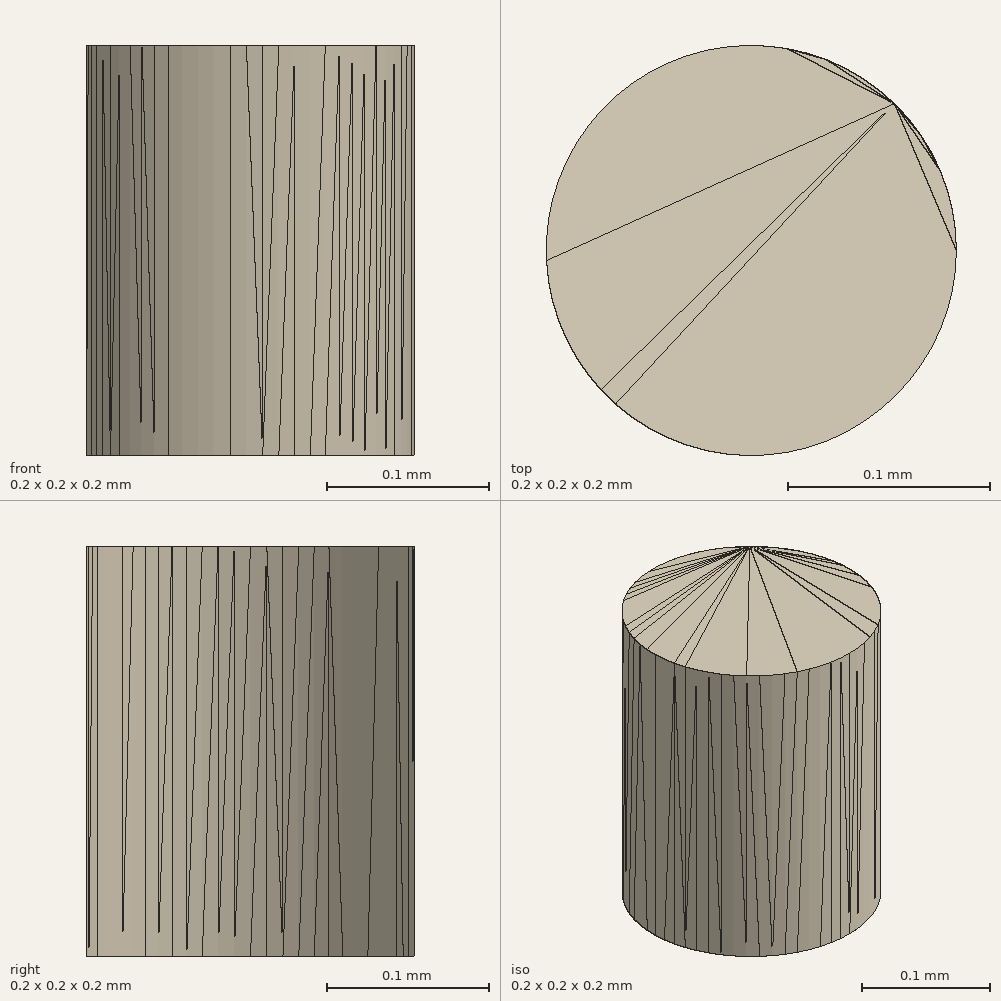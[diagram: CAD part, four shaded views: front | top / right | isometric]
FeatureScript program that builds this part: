
annotation { "Feature Type Name" : "Feature", "Feature Type Description" : "" }
export const myFeature = defineFeature(function(context is Context, id is Id, definition is map)
    precondition{}
    {
        {
            var Q0;
            Q0=qCreatedBy(makeId("Top.planeOp"),FACE);
            var sketch = newSketch(context, id + "F0", { "sketchPlane" : qUnion([Q0])});
            skCircle(sketch, "E0", {"center": v(0, 0) * mm, "radius": 0.1 * mm});
            skSolve(sketch);
        }
        {
            var Q0;
            Q0=makeQuery(id+"F0.imprint","IMPRINT",FACE,{"disambiguationData":[TD([[makeQuery(id+"F0.imprint","IMPRINT",EDGE,{"derivedFrom":sQuery(id+"F0.wireOp",EDGE,"E0")}),1.0]])]});
            extrude(context, id + "F1", {"entities" : qUnion([Q0]), "depth" : 0.25 * mm});
        }
        {
            var Q0;
            Q0=makeQuery(id+"F1.opExtrude","SWEPT_BODY",BODY,{"disambiguationData":[OSD([sQuery(id+"F0.wireOp",EDGE,"E0")])]});
            transform(context, id + "F2", {"entities" : qUnion([Q0]), "transformType" : TransformType.COPY});
        }
    });
